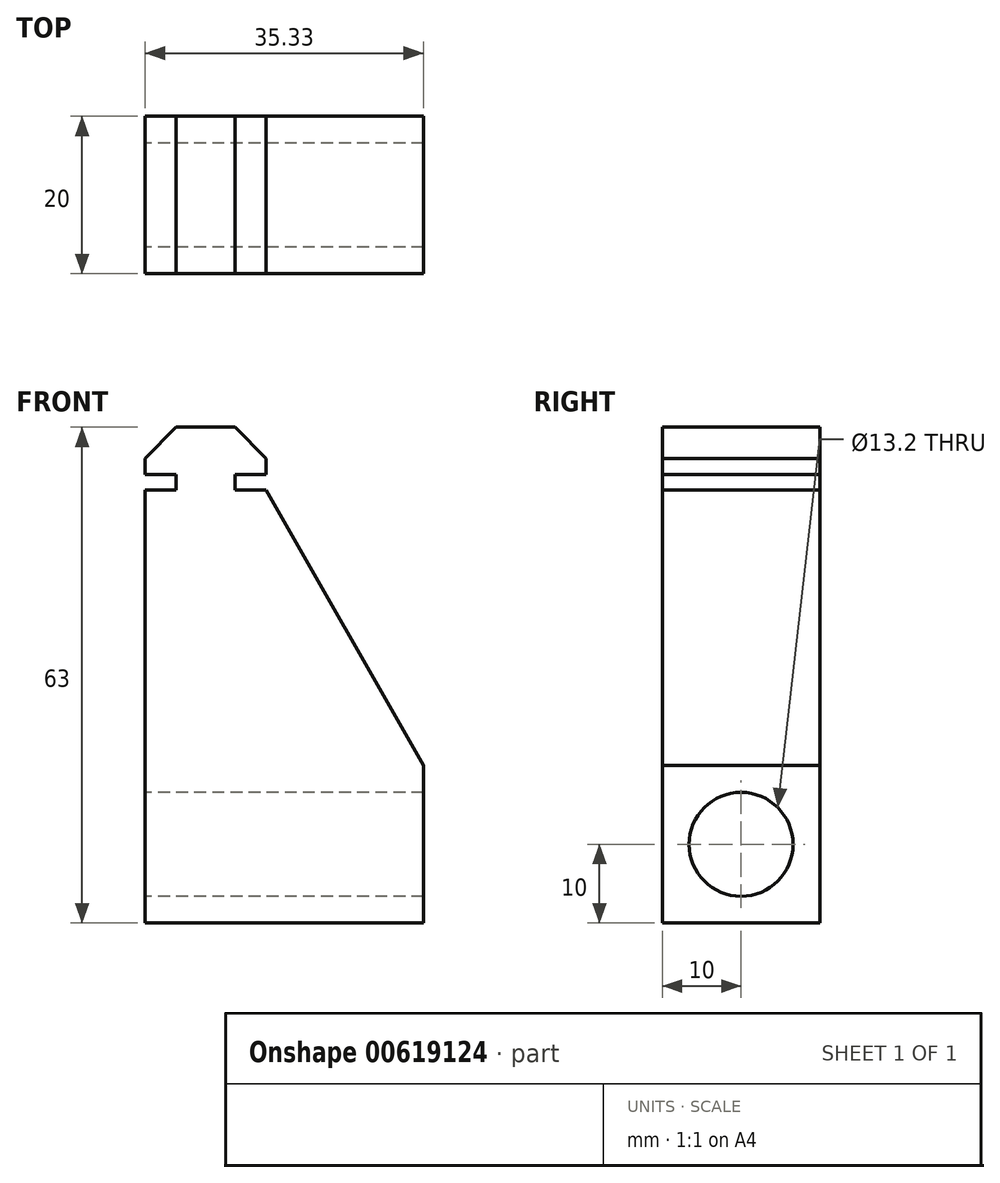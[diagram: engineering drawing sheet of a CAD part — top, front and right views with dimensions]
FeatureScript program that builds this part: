
annotation { "Feature Type Name" : "Feature", "Feature Type Description" : "" }
export const myFeature = defineFeature(function(context is Context, id is Id, definition is map)
    precondition{}
    {
        {
            var Q0;
            Q0=qCreatedBy(makeId("Front.planeOp"),FACE);
            var sketch = newSketch(context, id + "F0", { "sketchPlane" : qUnion([Q0])});
            skLineSegment(sketch, "E0", {"start": v(-4.96, 0) * mm, "end": v(-4.96, 2) * mm});
            skLineSegment(sketch, "E1", {"start": v(-4.96, 2) * mm, "end": v(-8.88, 2) * mm});
            skLineSegment(sketch, "E2", {"start": v(-8.88, 2) * mm, "end": v(-8.88, 4) * mm});
            skLineSegment(sketch, "E3", {"start": v(-8.88, 4) * mm, "end": v(-4.96, 8) * mm});
            skLineSegment(sketch, "E4", {"start": v(-4.96, 8) * mm, "end": v(2.54, 8) * mm});
            skLineSegment(sketch, "E5", {"start": v(2.54, 8) * mm, "end": v(6.45, 4) * mm});
            skLineSegment(sketch, "E6", {"start": v(6.45, 4) * mm, "end": v(6.45, 2) * mm});
            skLineSegment(sketch, "E7", {"start": v(6.45, 2) * mm, "end": v(2.54, 2) * mm});
            skLineSegment(sketch, "E8", {"start": v(2.54, 2) * mm, "end": v(2.54, 0) * mm});
            skLineSegment(sketch, "E9", {"start": v(2.54, 0) * mm, "end": v(-4.96, 0) * mm});
            skLineSegment(sketch, "E10.bottom", {"start": v(-8.88, 0) * mm, "end": v(6.45, 0) * mm});
            skLineSegment(sketch, "E10.top", {"start": v(-8.88, -55) * mm, "end": v(6.45, -55) * mm});
            skLineSegment(sketch, "E10.left", {"start": v(-8.88, 0) * mm, "end": v(-8.88, -55) * mm});
            skLineSegment(sketch, "E10.right", {"start": v(6.45, 0) * mm, "end": v(6.45, -55) * mm});
            skSolve(sketch);
        }
        {
            var Q0;
            Q0=qSketchRegion(id+"F0",true);
            extrude(context, id + "F1", {"entities" : qUnion([Q0]), "depth" : 20 * mm, "offsetDistance" : 25 * mm});
        }
        {
            var Q0;
            Q0=makeQuery(id+"F1.opExtrude","SWEPT_FACE",FACE,{"disambiguationData":[OSD([sQuery(id+"F0.wireOp",EDGE,"E10.right")])]});
            var sketch = newSketch(context, id + "F2", { "sketchPlane" : qUnion([Q0])});
            skLineSegment(sketch, "E11.bottom", {"start": v(-20, -55) * mm, "end": v(0, -55) * mm});
            skLineSegment(sketch, "E11.top", {"start": v(-20, -35) * mm, "end": v(0, -35) * mm});
            skLineSegment(sketch, "E11.left", {"start": v(-20, -55) * mm, "end": v(-20, -35) * mm});
            skLineSegment(sketch, "E11.right", {"start": v(0, -55) * mm, "end": v(0, -35) * mm});
            skSolve(sketch);
        }
        {
            var Q0;
            Q0 = qSketchRegion(id + "F2", true);
            extrude(context, id + "F3", {"entities" : qUnion([Q0]), "operationType" : NewBodyOperationType.ADD, "depth" : 20 * mm, "offsetDistance" : 25 * mm});
        }
        {
            var Q0;
            Q0=makeQuery(id+"F3.opExtrude","CAP_FACE",FACE,{"disambiguationData":[OSD([sQuery(id+"F2.wireOp",EDGE,"E11.bottom"),sQuery(id+"F2.wireOp",EDGE,"E11.top"),sQuery(id+"F2.wireOp",EDGE,"E11.left"),sQuery(id+"F2.wireOp",EDGE,"E11.right")])],"isStart":false});
            var sketch = newSketch(context, id + "F4", { "sketchPlane" : qUnion([Q0])});
            skPoint(sketch, "E12", {"position": v(-10, -45) * mm});
            skPoint(sketch, "E12.positionSnap0", {"position": v(0, -45) * mm});
            skPoint(sketch, "E12.positionSnap1", {"position": v(-10, -35) * mm});
            skSolve(sketch);
        }
        {
            var Q0;
            Q0=sQuery(id+"F4.wireOp",VERTEX,"E12");
            var Q1;
            Q1=makeQuery(id+"F1.opExtrude","SWEPT_BODY",BODY,{"disambiguationData":[OSD([sQuery(id+"F0.wireOp",EDGE,"E0"),sQuery(id+"F0.wireOp",EDGE,"E1"),sQuery(id+"F0.wireOp",EDGE,"E2"),sQuery(id+"F0.wireOp",EDGE,"E3"),sQuery(id+"F0.wireOp",EDGE,"E4"),sQuery(id+"F0.wireOp",EDGE,"E5"),sQuery(id+"F0.wireOp",EDGE,"E6"),sQuery(id+"F0.wireOp",EDGE,"E7"),sQuery(id+"F0.wireOp",EDGE,"E8"),sQuery(id+"F0.wireOp",EDGE,"E10.bottom"),sQuery(id+"F0.wireOp",EDGE,"E10.top"),sQuery(id+"F0.wireOp",EDGE,"E10.left"),sQuery(id+"F0.wireOp",EDGE,"E10.right")])]});
            hole(context, id + "F5", {"style" : HoleStyle.SIMPLE, "endStyle" : HoleEndStyle.THROUGH, "standardTappedOrClearance" : lookupTablePath({ "standard" : "ISO", "fit" : "Normal", "size" : "M12", "type" : "Clearance" }), "standardBlindInLast" : lookupTablePath({ "fit" : "Standard", "standard" : "ISO", "size" : "M12", "type" : "Clearance" }), "holeDiameter" : 13.2 * mm, "majorDiameter" : 5 * mm, "isTappedThrough" : true, "tappedDepth" : 12 * mm, "tapClearance" : 3, "locations" : qUnion([Q0]), "scope" : qUnion([Q1]), "startStyle" : HoleStartStyle.SKETCH});
        }
        {
            var Q0;
            Q0=makeQuery(id+"F3.boolean.opBoolean","MERGE",FACE,{"derivedFrom":[makeQuery(id+"F1.opExtrude","CAP_FACE",FACE,{"disambiguationData":[OSD([sQuery(id+"F0.wireOp",EDGE,"E0"),sQuery(id+"F0.wireOp",EDGE,"E1"),sQuery(id+"F0.wireOp",EDGE,"E2"),sQuery(id+"F0.wireOp",EDGE,"E3"),sQuery(id+"F0.wireOp",EDGE,"E4"),sQuery(id+"F0.wireOp",EDGE,"E5"),sQuery(id+"F0.wireOp",EDGE,"E6"),sQuery(id+"F0.wireOp",EDGE,"E7"),sQuery(id+"F0.wireOp",EDGE,"E8"),sQuery(id+"F0.wireOp",EDGE,"E10.bottom"),sQuery(id+"F0.wireOp",EDGE,"E10.top"),sQuery(id+"F0.wireOp",EDGE,"E10.left"),sQuery(id+"F0.wireOp",EDGE,"E10.right")])],"isStart":false}),makeQuery(id+"F3.opExtrude","SWEPT_FACE",FACE,{"disambiguationData":[OSD([sQuery(id+"F2.wireOp",EDGE,"E11.left")])]})]});
            var sketch = newSketch(context, id + "F6", { "sketchPlane" : qUnion([Q0])});
            skLineSegment(sketch, "E13", {"start": v(26.45, -35) * mm, "end": v(6.45, 0) * mm});
            skLineSegment(sketch, "E14", {"start": v(6.45, 0) * mm, "end": v(6.45, -35) * mm});
            skLineSegment(sketch, "E15", {"start": v(6.45, -35) * mm, "end": v(26.45, -35) * mm});
            skSolve(sketch);
        }
        {
            var Q0;
            Q0 = qSketchRegion(id + "F6", true);
            extrude(context, id + "F7", {"entities" : qUnion([Q0]), "operationType" : NewBodyOperationType.ADD, "oppositeDirection" : true, "depth" : 20 * mm, "offsetDistance" : 25 * mm});
        }
    });
